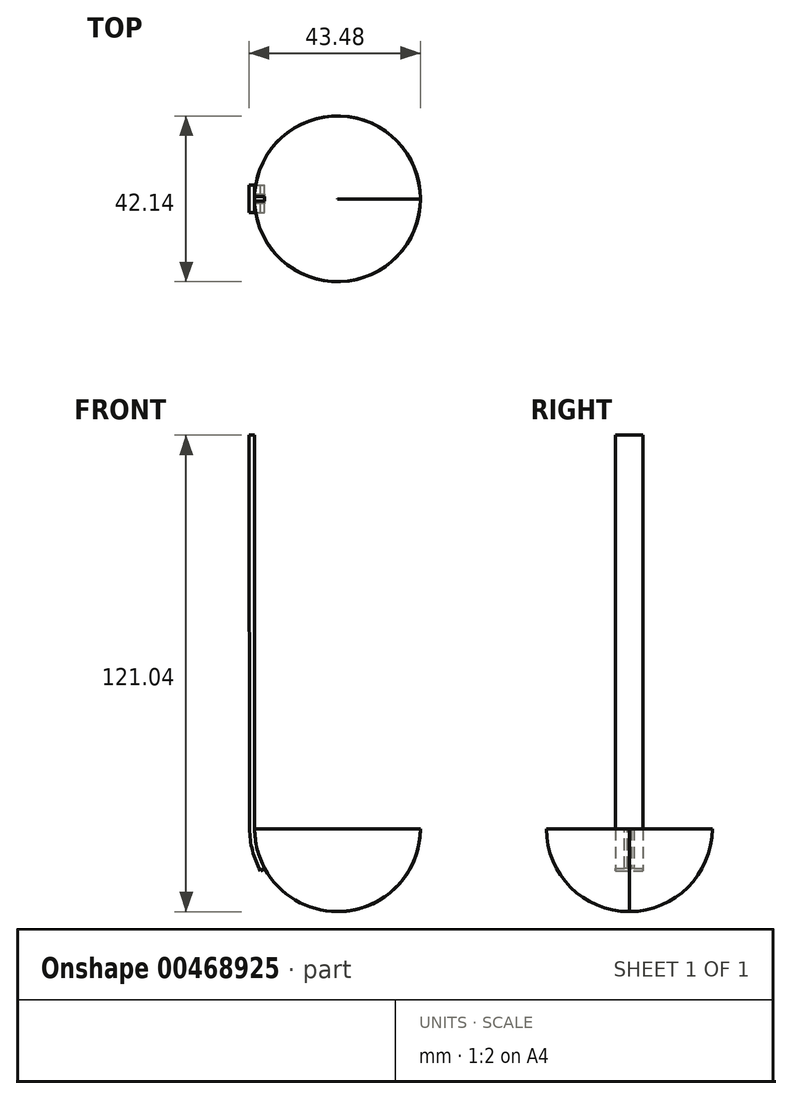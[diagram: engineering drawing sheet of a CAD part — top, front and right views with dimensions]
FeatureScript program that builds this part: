
annotation { "Feature Type Name" : "Feature", "Feature Type Description" : "" }
export const myFeature = defineFeature(function(context is Context, id is Id, definition is map)
    precondition{}
    {
        {
            var Q0;
            Q0=qCreatedBy(makeId("Front.planeOp"),FACE);
            var sketch = newSketch(context, id + "F0", { "sketchPlane" : qUnion([Q0])});
            skArc(sketch, "E0", {"start": v(0, -21.07) * mm, "mid": v(14.9, -14.9) * mm, "end": v(21.07, 0) * mm});
            skArc(sketch, "E1", {"start": v(0, -21.04) * mm, "mid": v(14.88, -14.88) * mm, "end": v(21.04, 0) * mm});
            skLineSegment(sketch, "E2", {"start": v(21.07, 0) * mm, "end": v(21.04, 0) * mm});
            skLineSegment(sketch, "E3", {"start": v(0, -21.04) * mm, "end": v(0, -21.07) * mm});
            skSolve(sketch);
        }
        {
            var Q0;
            Q0=qSketchRegion(id+"F0",true);
            extrude(context, id + "F1", {"entities" : qUnion([Q0]), "depth" : 0.01 * mm});
        }
        {
            var Q0;
            Q0=qCreatedBy(makeId("Top.planeOp"),FACE);
            var sketch = newSketch(context, id + "F2", { "sketchPlane" : qUnion([Q0])});
            skCircle(sketch, "E4", {"center": v(0, 0) * mm, "radius": 21.06 * mm});
            skSolve(sketch);
        }
        {
            var Q0;
            Q0=makeQuery(id+"F1.opExtrude","CAP_FACE",FACE,{"disambiguationData":[OSD([sQuery(id+"F0.wireOp",EDGE,"E0"),sQuery(id+"F0.wireOp",EDGE,"E1"),sQuery(id+"F0.wireOp",EDGE,"E2"),sQuery(id+"F0.wireOp",EDGE,"E3")])],"isStart":true});
            var Q1;
            Q1=sQuery(id+"F2.wireOp",EDGE,"E4");
            sweep(context, id + "F3", {"operationType" : NewBodyOperationType.ADD, "profiles" : qUnion([Q0]), "path" : qUnion([Q1])});
        }
        {
            var Q0;
            Q0=qCreatedBy(makeId("Front.planeOp"),FACE);
            var sketch = newSketch(context, id + "F4", { "sketchPlane" : qUnion([Q0])});
            skLineSegment(sketch, "E5", {"start": v(-21, 0) * mm, "end": v(-21, 99.97) * mm});
            skLineSegment(sketch, "E6", {"start": v(-22.41, 99.97) * mm, "end": v(-21, 99.97) * mm});
            skLineSegment(sketch, "E7", {"start": v(-22.41, 99.97) * mm, "end": v(-22.28, 0) * mm});
            skLineSegment(sketch, "E8", {"start": v(-21, 0) * mm, "end": v(-22.28, 0) * mm});
            skSolve(sketch);
        }
        {
            var Q0;
            Q0=qSketchRegion(id+"F4",true);
            extrude(context, id + "F5", {"entities" : qUnion([Q0]), "endBound" : BoundingType.SYMMETRIC, "depth" : 7 * mm});
        }
        {
            var Q0;
            Q0=qCreatedBy(makeId("Front.planeOp"),FACE);
            var sketch = newSketch(context, id + "F6", { "sketchPlane" : qUnion([Q0])});
            skArc(sketch, "E9", {"start": v(-21.03, 0) * mm, "mid": v(-20.38, -5.2) * mm, "end": v(-18.46, -10.08) * mm});
            skArc(sketch, "E10", {"start": v(-22.3, 0) * mm, "mid": v(-21.6, -5.55) * mm, "end": v(-19.53, -10.75) * mm});
            skLineSegment(sketch, "E11", {"start": v(-19.53, -10.75) * mm, "end": v(-18.46, -10.08) * mm});
            skLineSegment(sketch, "E12", {"start": v(-21.03, 0) * mm, "end": v(-22.3, 0) * mm});
            skSolve(sketch);
        }
        {
            var Q0;
            Q0=qSketchRegion(id+"F6",true);
            extrude(context, id + "F7", {"entities" : qUnion([Q0]), "operationType" : NewBodyOperationType.ADD, "endBound" : BoundingType.SYMMETRIC, "depth" : 7 * mm});
        }
    });
